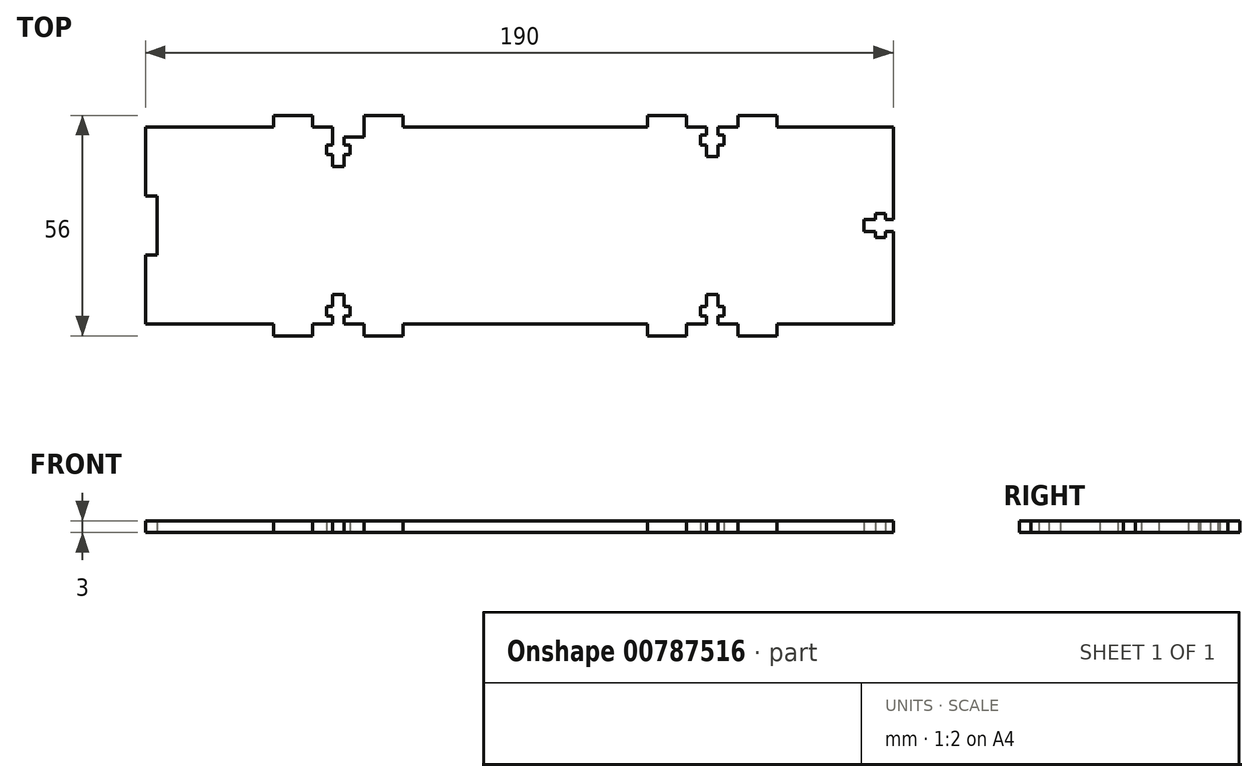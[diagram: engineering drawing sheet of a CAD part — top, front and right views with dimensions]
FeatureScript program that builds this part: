
annotation { "Feature Type Name" : "Feature", "Feature Type Description" : "" }
export const myFeature = defineFeature(function(context is Context, id is Id, definition is map)
    precondition{}
    {
        {
            var Q0;
            Q0=qCreatedBy(makeId("Top.planeOp"),FACE);
            var sketch = newSketch(context, id + "F0", { "sketchPlane" : qUnion([Q0])});
            skLineSegment(sketch, "E0.bottom", {"start": v(22.04, -19.54) * mm, "end": v(-7.46, -19.54) * mm});
            skLineSegment(sketch, "E0.top", {"start": v(22.04, -69.54) * mm, "end": v(-7.46, -69.54) * mm});
            skLineSegment(sketch, "E0.left", {"start": v(22.04, -19.54) * mm, "end": v(22.04, -43.04) * mm});
            skLineSegment(sketch, "E0.right", {"start": v(-167.96, -19.54) * mm, "end": v(-167.96, -37.04) * mm});
            skLineSegment(sketch, "E1", {"start": v(-118.96, -19.54) * mm, "end": v(-118.96, -69.54) * mm, "construction": true});
            skLineSegment(sketch, "E2", {"start": v(-23.96, -19.54) * mm, "end": v(-23.96, -69.54) * mm, "construction": true});
            skLineSegment(sketch, "E3", {"start": v(-22.46, -19.54) * mm, "end": v(-22.46, -21.54) * mm});
            skLineSegment(sketch, "E4", {"start": v(-22.46, -21.54) * mm, "end": v(-20.96, -21.54) * mm});
            skLineSegment(sketch, "E5", {"start": v(-20.96, -21.54) * mm, "end": v(-20.96, -24.04) * mm});
            skLineSegment(sketch, "E6", {"start": v(-20.96, -24.04) * mm, "end": v(-22.46, -24.04) * mm});
            skLineSegment(sketch, "E7", {"start": v(-22.46, -24.04) * mm, "end": v(-22.46, -27.04) * mm});
            skLineSegment(sketch, "E8", {"start": v(-22.46, -27.04) * mm, "end": v(-25.46, -27.04) * mm});
            skLineSegment(sketch, "E9", {"start": v(-25.46, -27.04) * mm, "end": v(-25.46, -24.04) * mm});
            skLineSegment(sketch, "E10", {"start": v(-25.46, -24.04) * mm, "end": v(-26.96, -24.04) * mm});
            skLineSegment(sketch, "E11", {"start": v(-26.96, -24.04) * mm, "end": v(-26.96, -21.54) * mm});
            skLineSegment(sketch, "E12", {"start": v(-26.96, -21.54) * mm, "end": v(-25.46, -21.54) * mm});
            skLineSegment(sketch, "E13", {"start": v(-25.46, -21.54) * mm, "end": v(-25.46, -19.54) * mm});
            skLineSegment(sketch, "E14.trimOffspring", {"start": v(-25.46, -19.54) * mm, "end": v(-30.46, -19.54) * mm});
            skLineSegment(sketch, "E15", {"start": v(-17.46, -19.54) * mm, "end": v(-17.46, -16.54) * mm});
            skLineSegment(sketch, "E16", {"start": v(-17.46, -16.54) * mm, "end": v(-7.46, -16.54) * mm});
            skLineSegment(sketch, "E17", {"start": v(-7.46, -16.54) * mm, "end": v(-7.46, -19.54) * mm});
            skLineSegment(sketch, "E18.trimOffspring", {"start": v(-17.46, -19.54) * mm, "end": v(-22.46, -19.54) * mm});
            skLineSegment(sketch, "E19", {"start": v(-30.46, -19.54) * mm, "end": v(-30.46, -16.54) * mm});
            skLineSegment(sketch, "E20", {"start": v(-30.46, -16.54) * mm, "end": v(-40.46, -16.54) * mm});
            skLineSegment(sketch, "E21", {"start": v(-40.46, -16.54) * mm, "end": v(-40.46, -19.54) * mm});
            skLineSegment(sketch, "E22.trimOffspring", {"start": v(-40.46, -19.54) * mm, "end": v(-102.46, -19.54) * mm});
            skLineSegment(sketch, "E23", {"start": v(-117.46, -22.04) * mm, "end": v(-117.46, -24.04) * mm});
            skLineSegment(sketch, "E24", {"start": v(-117.46, -24.04) * mm, "end": v(-115.96, -24.04) * mm});
            skLineSegment(sketch, "E25", {"start": v(-115.96, -24.04) * mm, "end": v(-115.96, -26.54) * mm});
            skLineSegment(sketch, "E26", {"start": v(-115.96, -26.54) * mm, "end": v(-117.46, -26.54) * mm});
            skLineSegment(sketch, "E27", {"start": v(-117.46, -26.54) * mm, "end": v(-117.46, -29.54) * mm});
            skLineSegment(sketch, "E28", {"start": v(-117.46, -29.54) * mm, "end": v(-120.46, -29.54) * mm});
            skLineSegment(sketch, "E29", {"start": v(-120.46, -29.54) * mm, "end": v(-120.46, -26.54) * mm});
            skLineSegment(sketch, "E30", {"start": v(-120.46, -26.54) * mm, "end": v(-121.96, -26.54) * mm});
            skLineSegment(sketch, "E31", {"start": v(-121.96, -26.54) * mm, "end": v(-121.96, -24.04) * mm});
            skLineSegment(sketch, "E32", {"start": v(-121.96, -24.04) * mm, "end": v(-120.46, -24.04) * mm});
            skLineSegment(sketch, "E33", {"start": v(-120.46, -24.04) * mm, "end": v(-120.46, -19.54) * mm});
            skLineSegment(sketch, "E34", {"start": v(-112.46, -22.04) * mm, "end": v(-112.46, -16.54) * mm});
            skLineSegment(sketch, "E35", {"start": v(-112.46, -16.54) * mm, "end": v(-102.46, -16.54) * mm});
            skLineSegment(sketch, "E36", {"start": v(-102.46, -16.54) * mm, "end": v(-102.46, -19.54) * mm});
            skLineSegment(sketch, "E37", {"start": v(-125.46, -19.54) * mm, "end": v(-125.46, -16.54) * mm});
            skLineSegment(sketch, "E38", {"start": v(-125.46, -16.54) * mm, "end": v(-135.46, -16.54) * mm});
            skLineSegment(sketch, "E39", {"start": v(-135.46, -16.54) * mm, "end": v(-135.46, -19.54) * mm});
            skLineSegment(sketch, "E40.trimOffspring", {"start": v(-135.46, -19.54) * mm, "end": v(-167.96, -19.54) * mm});
            skLineSegment(sketch, "E41.trimOffspring", {"start": v(-120.46, -19.54) * mm, "end": v(-125.46, -19.54) * mm});
            skLineSegment(sketch, "E42", {"start": v(-117.46, -22.04) * mm, "end": v(-112.46, -22.04) * mm});
            skLineSegment(sketch, "E43", {"start": v(-120.46, -69.54) * mm, "end": v(-120.46, -67.54) * mm});
            skLineSegment(sketch, "E44", {"start": v(-120.46, -67.54) * mm, "end": v(-121.96, -67.54) * mm});
            skLineSegment(sketch, "E45", {"start": v(-121.96, -67.54) * mm, "end": v(-121.96, -65.04) * mm});
            skLineSegment(sketch, "E46", {"start": v(-121.96, -65.04) * mm, "end": v(-120.46, -65.04) * mm});
            skLineSegment(sketch, "E47", {"start": v(-120.46, -65.04) * mm, "end": v(-120.46, -62.04) * mm});
            skLineSegment(sketch, "E48", {"start": v(-120.46, -62.04) * mm, "end": v(-117.46, -62.04) * mm});
            skLineSegment(sketch, "E49", {"start": v(-117.46, -62.04) * mm, "end": v(-117.46, -65.04) * mm});
            skLineSegment(sketch, "E50", {"start": v(-117.46, -65.04) * mm, "end": v(-115.96, -65.04) * mm});
            skLineSegment(sketch, "E51", {"start": v(-115.96, -65.04) * mm, "end": v(-115.96, -67.54) * mm});
            skLineSegment(sketch, "E52", {"start": v(-115.96, -67.54) * mm, "end": v(-117.46, -67.54) * mm});
            skLineSegment(sketch, "E53", {"start": v(-117.46, -67.54) * mm, "end": v(-117.46, -69.54) * mm});
            skLineSegment(sketch, "E54", {"start": v(-125.46, -69.54) * mm, "end": v(-125.46, -72.54) * mm});
            skLineSegment(sketch, "E55", {"start": v(-125.46, -72.54) * mm, "end": v(-135.46, -72.54) * mm});
            skLineSegment(sketch, "E56", {"start": v(-135.46, -72.54) * mm, "end": v(-135.46, -69.54) * mm});
            skLineSegment(sketch, "E57", {"start": v(-112.46, -69.54) * mm, "end": v(-112.46, -72.54) * mm});
            skLineSegment(sketch, "E58", {"start": v(-112.46, -72.54) * mm, "end": v(-102.46, -72.54) * mm});
            skLineSegment(sketch, "E59", {"start": v(-102.46, -72.54) * mm, "end": v(-102.46, -69.54) * mm});
            skLineSegment(sketch, "E60.trimOffspring", {"start": v(-135.46, -69.54) * mm, "end": v(-167.96, -69.54) * mm});
            skLineSegment(sketch, "E61.trimOffspring", {"start": v(-120.46, -69.54) * mm, "end": v(-125.46, -69.54) * mm});
            skLineSegment(sketch, "E62.trimOffspring", {"start": v(-112.46, -69.54) * mm, "end": v(-117.46, -69.54) * mm});
            skLineSegment(sketch, "E63", {"start": v(-25.46, -69.54) * mm, "end": v(-25.46, -67.54) * mm});
            skLineSegment(sketch, "E64", {"start": v(-25.46, -67.54) * mm, "end": v(-26.96, -67.54) * mm});
            skLineSegment(sketch, "E65", {"start": v(-26.96, -67.54) * mm, "end": v(-26.96, -65.04) * mm});
            skLineSegment(sketch, "E66", {"start": v(-26.96, -65.04) * mm, "end": v(-25.46, -65.04) * mm});
            skLineSegment(sketch, "E67", {"start": v(-25.46, -65.04) * mm, "end": v(-25.46, -62.04) * mm});
            skLineSegment(sketch, "E68", {"start": v(-25.46, -62.04) * mm, "end": v(-22.46, -62.04) * mm});
            skLineSegment(sketch, "E69", {"start": v(-22.46, -62.04) * mm, "end": v(-22.46, -65.04) * mm});
            skLineSegment(sketch, "E70", {"start": v(-22.46, -65.04) * mm, "end": v(-20.96, -65.04) * mm});
            skLineSegment(sketch, "E71", {"start": v(-20.96, -65.04) * mm, "end": v(-20.96, -67.54) * mm});
            skLineSegment(sketch, "E72", {"start": v(-20.96, -67.54) * mm, "end": v(-22.46, -67.54) * mm});
            skLineSegment(sketch, "E73", {"start": v(-22.46, -67.54) * mm, "end": v(-22.46, -69.54) * mm});
            skLineSegment(sketch, "E74", {"start": v(-30.46, -69.54) * mm, "end": v(-30.46, -72.54) * mm});
            skLineSegment(sketch, "E75", {"start": v(-30.46, -72.54) * mm, "end": v(-40.46, -72.54) * mm});
            skLineSegment(sketch, "E76", {"start": v(-40.46, -72.54) * mm, "end": v(-40.46, -69.54) * mm});
            skLineSegment(sketch, "E77", {"start": v(-17.46, -69.54) * mm, "end": v(-17.46, -72.54) * mm});
            skLineSegment(sketch, "E78", {"start": v(-17.46, -72.54) * mm, "end": v(-7.46, -72.54) * mm});
            skLineSegment(sketch, "E79", {"start": v(-7.46, -72.54) * mm, "end": v(-7.46, -69.54) * mm});
            skLineSegment(sketch, "E80.trimOffspring", {"start": v(-40.46, -69.54) * mm, "end": v(-102.46, -69.54) * mm});
            skLineSegment(sketch, "E81.trimOffspring", {"start": v(-25.46, -69.54) * mm, "end": v(-30.46, -69.54) * mm});
            skLineSegment(sketch, "E82.trimOffspring", {"start": v(-17.46, -69.54) * mm, "end": v(-22.46, -69.54) * mm});
            skLineSegment(sketch, "E83.bottom", {"start": v(-164.96, -37.04) * mm, "end": v(-167.96, -37.04) * mm});
            skLineSegment(sketch, "E83.top", {"start": v(-164.96, -52.04) * mm, "end": v(-167.96, -52.04) * mm});
            skLineSegment(sketch, "E83.left", {"start": v(-164.96, -37.04) * mm, "end": v(-164.96, -52.04) * mm});
            skPoint(sketch, "E83.middle", {"position": v(-167.96, -44.54) * mm});
            skLineSegment(sketch, "E84.trimOffspring", {"start": v(-167.96, -52.04) * mm, "end": v(-167.96, -69.54) * mm});
            skLineSegment(sketch, "E85", {"start": v(22.04, -46.04) * mm, "end": v(20.04, -46.04) * mm});
            skLineSegment(sketch, "E86", {"start": v(20.04, -46.04) * mm, "end": v(20.04, -47.54) * mm});
            skLineSegment(sketch, "E87", {"start": v(20.04, -47.54) * mm, "end": v(17.54, -47.54) * mm});
            skLineSegment(sketch, "E88", {"start": v(17.54, -47.54) * mm, "end": v(17.54, -46.04) * mm});
            skLineSegment(sketch, "E89", {"start": v(17.54, -46.04) * mm, "end": v(14.54, -46.04) * mm});
            skLineSegment(sketch, "E90", {"start": v(14.54, -46.04) * mm, "end": v(14.54, -43.04) * mm});
            skLineSegment(sketch, "E91", {"start": v(14.54, -43.04) * mm, "end": v(17.54, -43.04) * mm});
            skLineSegment(sketch, "E92", {"start": v(17.54, -43.04) * mm, "end": v(17.54, -41.54) * mm});
            skLineSegment(sketch, "E93", {"start": v(17.54, -41.54) * mm, "end": v(20.04, -41.54) * mm});
            skLineSegment(sketch, "E94", {"start": v(20.04, -41.54) * mm, "end": v(20.04, -43.04) * mm});
            skLineSegment(sketch, "E95", {"start": v(20.04, -43.04) * mm, "end": v(22.04, -43.04) * mm});
            skLineSegment(sketch, "E96.trimOffspring", {"start": v(22.04, -46.04) * mm, "end": v(22.04, -69.54) * mm});
            skSolve(sketch);
        }
        {
            var Q0;
            Q0=makeQuery(id+"F0.imprint","IMPRINT",FACE,{"disambiguationData":[TD([[makeQuery(id+"F0.imprint","IMPRINT",EDGE,{"derivedFrom":sQuery(id+"F0.wireOp",EDGE,"E0.bottom")}),1.0]])]});
            extrude(context, id + "F1", {"entities" : qUnion([Q0]), "depth" : 3 * mm, "offsetDistance" : 25.4 * mm});
        }
    });
